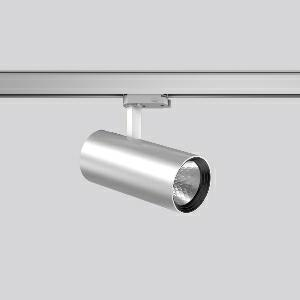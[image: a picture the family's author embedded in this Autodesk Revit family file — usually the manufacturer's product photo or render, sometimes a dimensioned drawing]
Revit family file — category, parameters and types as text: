
# Revit family: deecos_s_mini_742197_004_1_76_e00e
name_source: partatom
category: Lighting Fixtures
units: mm (PartAtom-declared; Revit-internal decimal feet)

## family parameters
Cut with Voids When Loaded = No
Host = Face
Light Source = No
Part Type = Normal
Room Calculation Point = No
Round Connector Dimension = Use Diameter
Shared = No

## types (1)
- DEECOS S mini (1 x LED Modul 940, 2750 lm, 4000)
    Apparent Load = 20 VA
    Approval mark = CE
    CIE Flux Codes = 95 99 100 100 100
    Color Rendering = 92
    Color Temperature = 4000
    Default Elevation = 1800 mm
    Description = Series: DEECOS S mini
LED surface-mounted projector in modern design with no visible cooling ribs. Housing: die-cast aluminium, powder-coated. Rotation range: 356°. Swivel range: 90°. Black plastic ring and recessed LED to prevent glare from the side. Optical assembly with reflector made of MIRO-Silver with 98% total light reflection for outstanding efficiency - can be changed without tools. Best colour rendering index Ra>90. With adapter for RZB 3-circuit DALI tracks. Suitable for Track on ceiling, Wall track. High quality converter without flickering and stroboscopic effect. The following accessories can be mounted without use of tools: interchangeable lenses, decorative glasses, honeycomb louvre, clear and frosted diffusers, white interchangeable plastic ring. 
Colour: silver
Diameter: 87 mm
Height: 214 mm
Lamp: LED
Socket: without socket
Colour temperature: 4000K
Colour rendering index (CRI): 92
System power: 20 W
Rated luminous flux: 2750 lm
Luminous efficiency: 138 lm/W
Control gear: Converter, dimmable, DALI
Protection class: I
Type of protection: IP 20
    Height = 214 mm
    Lamp = 1 x LED Modul 940
    Lamp Light Flux = 2750 lm
    Lamp count = 1
    Length = 87 mm
    Lifetime = 50000 h
    Luminous efficacy = 138 lm/W
    Manufacturer = RZB
    ModVariant = No
    Model = 742197.004.1.76
    Mounting Place = Ceiling
    Mounting Type = Rail mounted
    Number of Poles = 1
    OnlyDefault = Yes
    Power Factor = 1
    Product Name = DEECOS S mini
    Product group = Track mounted projectors
    ProductGroupID = 301
    Protection Class = Protection class I
    Protection Degree = IP 20
    RLX_Detail_Level = 1
    RLX_Emergency_Light_Flux = 0 lm
    RLX_Emergency_Type = 0
    RLX_Emergency_Type_DB = No
    RlxData = <blob elided: 37101 chars, md5=6c6655bc>
    Socket = socket
    Standby Power = 0 W
    System Light Flux = 2750 lm
    System Power = 20 W
    Type Comments = Product without accessories
    Type Image = 741926.004.jpg
    URL = http://relux.com
    VarID = ---
    Voltage = 230 V
    Voltage Range = 220-240 V
    Weight = 0.00 kg
    Width = 0 mm  [stored 0 ft]

note: [stored X ft] marks values corroborated as IEEE doubles in the binary element streams (Revit-internal decimal feet)

## geometry (parser evidence)
native form markers: Blend x4, Sweep x11
no freeform markers — native parametric forms only
